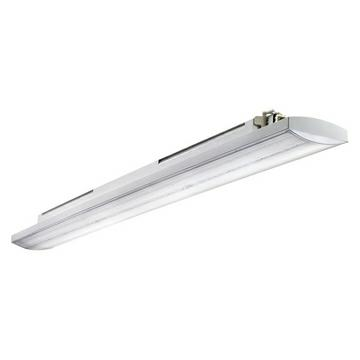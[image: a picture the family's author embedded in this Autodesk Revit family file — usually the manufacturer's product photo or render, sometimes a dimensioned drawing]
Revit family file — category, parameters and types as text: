
# Revit family: Lighting-Industriale-GEWISS-SMART[3]PLUS-PLAFONIERA-LED-EMERGENZA_TRANSPARENTE_1200mm
name_source: partatom
category: Apparecchi per illuminazione
units: mm (PartAtom-declared; Revit-internal decimal feet)

## family parameters
Condiviso = No
Host = Superficie
Punto di calcolo locali = No
Quota connettore circolare = Usa diametro
Sorgente d'illuminazione = No
Taglio con vuoti quando caricato = No
Tipo di parte = Normale

## types (1)
- Lighting-Industriale-GEWISS-SMART[3]PLUS-PLAFONIERA-LED-EMERGENZA_TRANSPARENTE_1200mm
    Applicazione = Interno
    Carico apparente = 56 VA
    Catalogo = LIGHTING
    Catalogo Serie = SMART[3] PLUS
    Classe di efficienza LED integrati = A ÷ A++
    Classe isolamento = II
    Codice Electrocod = 2434
    Commenti sul wattaggio = 56W
    Descrizione = SMART3 PLUS 1200 EMERG DT1+DT6 HE TRASP 9 57
    Ganci = GEWISS  - ALLUMINIO
    Garanzia = ND
    Glow Wire Test = 850°C
    Grado di protezione = IP66/IP69
    IDF = 587b6aa6-0e26-4fba-a401-9b2419879337
    IDT = 4cee24bc-7d08-4ab8-ad84-39fd04b56e2f
    Immagine tipo = GWS3136T.jpg
    Lampada = LED
    Lampada: = LED
    Lumen output (lm) = 4500
    Lunghezza = 1200 mm
    Lunghezza Lampada = 1200 mm
    Modello = GWS3225AT957
    Potenza di sistema = 36 W
    Produttore = GEWISS S.p.A.
    Prospetto di default = 1219 mm
    Resistenza agli urti = IK08
    SEO = Plafoniera
    Scheda Tecnica = https://www.gewiss.com
    Schermo = Trasparente
    Schermo. = Gewiss - Led Acceso
    Stampa 1_100 = Sì
    Stampa 1_200 = No
    Struttura = GEWISS - SMART 3 - GRIGIO
    Temperatura di colore = 5700 K (CRI > 90)
    Temperatura di colore: = 5700 K (CRI > 90)
    Temperatura di funzionamento = ND
    Temperatura di utilizzo = ND
    Tensione = 220-240 V
    Tipologia sorgente luminosa = LED - Non sostituibile
    URL = https://www.gewiss.com
    Versione file RFA = 20.0
